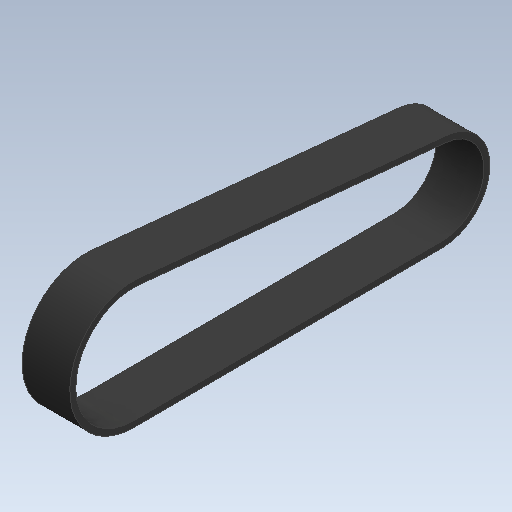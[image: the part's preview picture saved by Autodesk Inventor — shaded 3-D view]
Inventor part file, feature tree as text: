
AUTODESK INVENTOR PART (.ipt)
format: ipt  version: 2020 (Build 240168000, 168)  size: 107,520 bytes
history: native  units: mm
features: other x1, extrude x1, sketch x1
ambient origin geometry x8: Origin, YZ Plane, XZ Plane, XY Plane, X Axis, Y Axis, Z Axis, Center Point
bodies: Body1 (feature_tree)
feature tree (3):
  other  "Твердое тело1"
  extrude  "Выдавливание1"  Depth=38.872mm
  sketch  "Эскиз1"
